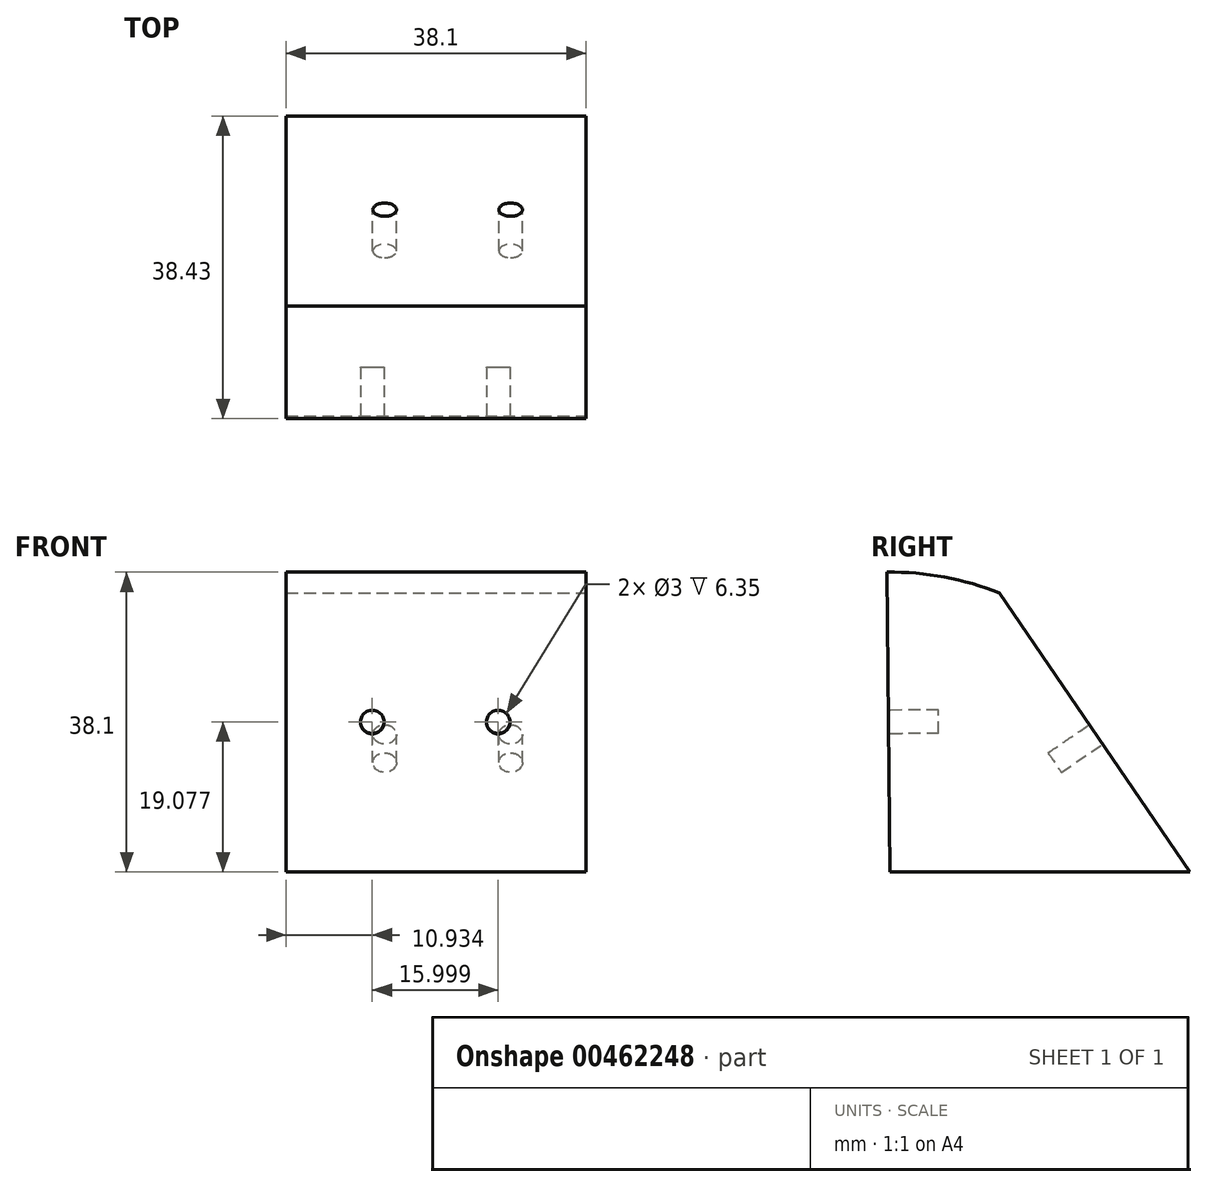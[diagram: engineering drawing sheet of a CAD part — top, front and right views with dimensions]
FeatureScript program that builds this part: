
annotation { "Feature Type Name" : "Feature", "Feature Type Description" : "" }
export const myFeature = defineFeature(function(context is Context, id is Id, definition is map)
    precondition{}
    {
        {
            var Q0;
            Q0=qCreatedBy(makeId("Top.planeOp"),FACE);
            var sketch = newSketch(context, id + "F0", { "sketchPlane" : qUnion([Q0])});
            skLineSegment(sketch, "E0.bottom", {"start": v(-18.58, 21.72) * mm, "end": v(19.52, 21.72) * mm});
            skLineSegment(sketch, "E0.top", {"start": v(-18.58, -16.38) * mm, "end": v(19.52, -16.38) * mm});
            skLineSegment(sketch, "E0.left", {"start": v(-18.58, 21.72) * mm, "end": v(-18.58, -16.38) * mm});
            skLineSegment(sketch, "E0.right", {"start": v(19.52, 21.72) * mm, "end": v(19.52, -16.38) * mm});
            skSolve(sketch);
        }
        {
            var Q0;
            Q0=makeQuery(id+"F0.imprint","IMPRINT",FACE,{"disambiguationData":[TD([[makeQuery(id+"F0.imprint","IMPRINT",EDGE,{"derivedFrom":sQuery(id+"F0.wireOp",EDGE,"E0.bottom")}),-1.0]])]});
            var Q1;
            Q1=sQuery(id+"F0.wireOp",EDGE,"E0.top");
            revolve(context, id + "F1", {"entities" : qUnion([Q0]), "axis" : qUnion([Q1]), "revolveType" : RevolveType.ONE_DIRECTION, "angle" : 68.5 * degree});
        }
        {
            var Q0;
            Q0=makeQuery(id+"F1.opRevolve","SWEPT_FACE",FACE,{"disambiguationData":[OSD([sQuery(id+"F0.wireOp",EDGE,"E0.left")])]});
            var sketch = newSketch(context, id + "F2", { "sketchPlane" : qUnion([Q0])});
            skLineSegment(sketch, "E1", {"start": v(2.42, 35.45) * mm, "end": v(-21.72, 0) * mm});
            skSolve(sketch);
        }
        {
            var Q0;
            Q0=makeQuery(id+"F2.imprint","IMPRINT",FACE,{"disambiguationData":[TD([[makeQuery(id+"F2.imprint","IMPRINT",EDGE,{"derivedFrom":sQuery(id+"F2.wireOp",EDGE,"E1")}),-1.0]])]});
            extrude(context, id + "F3", {"entities" : qUnion([Q0]), "operationType" : NewBodyOperationType.REMOVE, "endBound" : BoundingType.THROUGH_ALL, "oppositeDirection" : true, "depth" : 25.4 * mm, "offsetDistance" : 25.4 * mm});
        }
        {
            var Q0;
            Q0=makeQuery(id+"F1.opRevolve","CAP_FACE",FACE,{"disambiguationData":[OSD([sQuery(id+"F0.wireOp",EDGE,"E0.bottom"),sQuery(id+"F0.wireOp",EDGE,"E0.top"),sQuery(id+"F0.wireOp",EDGE,"E0.left"),sQuery(id+"F0.wireOp",EDGE,"E0.right")])],"isStart":false});
            var Q1;
            Q1=makeQuery(id+"F1.opRevolve","CAP_EDGE",EDGE,{"disambiguationData":[OSD([sQuery(id+"F0.wireOp",EDGE,"E0.top")])],"isStart":true});
            revolve(context, id + "F4", {"operationType" : NewBodyOperationType.ADD, "entities" : qUnion([Q0]), "axis" : qUnion([Q1]), "revolveType" : RevolveType.ONE_DIRECTION, "angle" : 22 * degree});
        }
        {
            var Q0;
            Q0=makeQuery(id+"F4.opRevolve","CAP_FACE",FACE,{"disambiguationData":[OSD([sQuery(id+"F0.wireOp",EDGE,"E0.bottom"),sQuery(id+"F0.wireOp",EDGE,"E0.top"),sQuery(id+"F0.wireOp",EDGE,"E0.left"),sQuery(id+"F0.wireOp",EDGE,"E0.right")])],"isStart":false});
            var sketch = newSketch(context, id + "F5", { "sketchPlane" : qUnion([Q0])});
            skCircle(sketch, "E2", {"center": v(-7.65, 19.2) * mm, "radius": 1.5 * mm});
            skCircle(sketch, "E3.1.0.0", {"center": v(8.35, 19.2) * mm, "radius": 1.5 * mm});
            skLineSegment(sketch, "E3.direction1", {"start": v(-7.65, 19.2) * mm, "end": v(8.35, 19.2) * mm, "construction": true});
            skSolve(sketch);
        }
        {
            var Q0;
            Q0=makeQuery(id+"F5.imprint","IMPRINT",FACE,{"disambiguationData":[TD([[makeQuery(id+"F5.imprint","IMPRINT",EDGE,{"derivedFrom":sQuery(id+"F5.wireOp",EDGE,"E2")}),-1.0]])]});
            var sketch = newSketch(context, id + "F6", { "sketchPlane" : qUnion([Q0])});
            skCircle(sketch, "E4", {"center": v(12.6, 36.51) * mm, "radius": 1.67 * mm});
            skSolve(sketch);
        }
        {
            var Q0;
            Q0=makeQuery(id+"F5.imprint","IMPRINT",FACE,{"disambiguationData":[TD([[makeQuery(id+"F5.imprint","IMPRINT",EDGE,{"derivedFrom":sQuery(id+"F5.wireOp",EDGE,"E2")}),1.0]])]});
            var Q1;
            Q1=makeQuery(id+"F6.imprint","IMPRINT",FACE,{"disambiguationData":[TD([[makeQuery(id+"F6.imprint","IMPRINT",EDGE,{"derivedFrom":makeQuery(id+"F5.imprint","IMPRINT",EDGE,{"derivedFrom":sQuery(id+"F5.wireOp",EDGE,"E3.1.0.0")})}),1.0]])]});
            extrude(context, id + "F7", {"entities" : qUnion([Q0, Q1]), "operationType" : NewBodyOperationType.REMOVE, "oppositeDirection" : true, "depth" : 6.35 * mm, "offsetDistance" : 25.4 * mm});
        }
        {
            var Q0;
            Q0=makeQuery(id+"F3.boolean.opBoolean","COPY",FACE,{"derivedFrom":makeQuery(id+"F3.opExtrude","SWEPT_FACE",FACE,{"disambiguationData":[OSD([sQuery(id+"F2.wireOp",EDGE,"E1")])]})});
            var sketch = newSketch(context, id + "F8", { "sketchPlane" : qUnion([Q0])});
            skCircle(sketch, "E5", {"center": v(-9.93, 8.9) * mm, "radius": 1.5 * mm});
            skCircle(sketch, "E6", {"center": v(6.07, 8.9) * mm, "radius": 1.5 * mm});
            skSolve(sketch);
        }
        {
            var Q0;
            Q0 = qSketchRegion(id + "F8", true);
            extrude(context, id + "F9", {"entities" : qUnion([Q0]), "operationType" : NewBodyOperationType.REMOVE, "oppositeDirection" : true, "depth" : 6.35 * mm, "offsetDistance" : 25.4 * mm});
        }
    });
